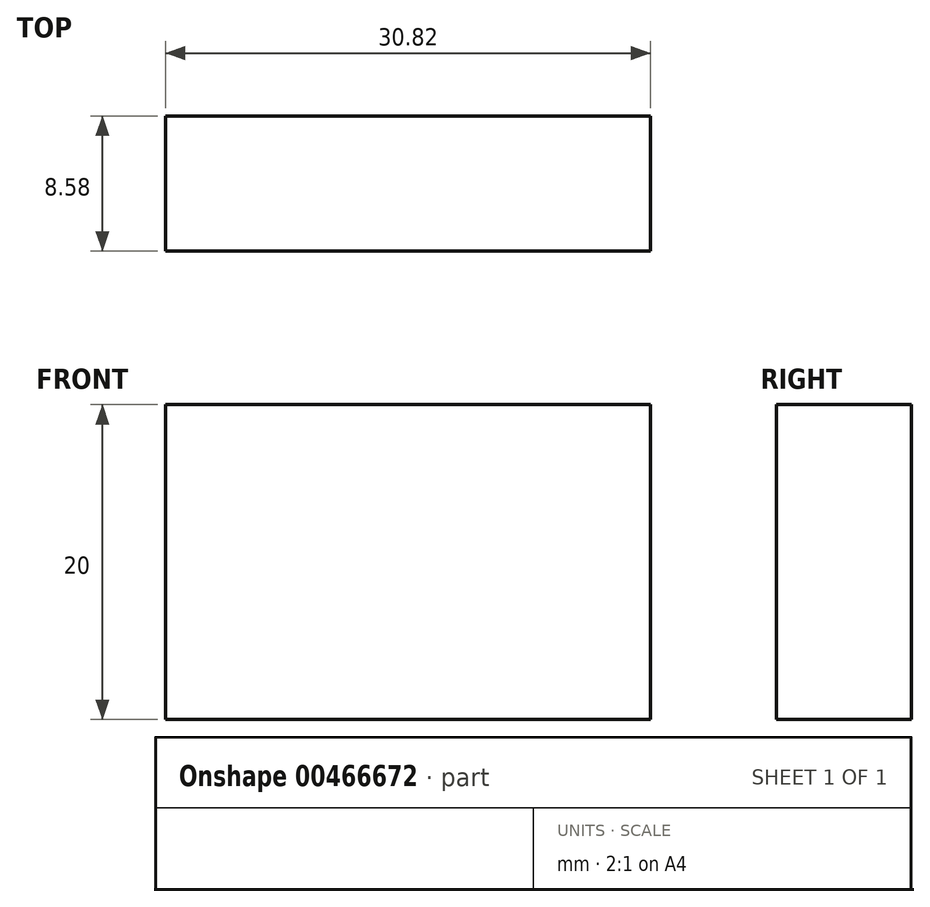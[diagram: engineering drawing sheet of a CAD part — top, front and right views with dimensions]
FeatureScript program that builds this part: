
annotation { "Feature Type Name" : "Feature", "Feature Type Description" : "" }
export const myFeature = defineFeature(function(context is Context, id is Id, definition is map)
    precondition{}
    {
        {
            var Q0;
            Q0=qCreatedBy(makeId("Top.planeOp"),FACE);
            var sketch = newSketch(context, id + "F0", { "sketchPlane" : qUnion([Q0])});
            skLineSegment(sketch, "E0.bottom", {"start": v(-15.4, 4.3) * mm, "end": v(15.4, 4.3) * mm});
            skLineSegment(sketch, "E0.top", {"start": v(-15.4, -4.3) * mm, "end": v(15.4, -4.3) * mm});
            skLineSegment(sketch, "E0.left", {"start": v(-15.4, 4.3) * mm, "end": v(-15.4, -4.3) * mm});
            skLineSegment(sketch, "E0.right", {"start": v(15.4, 4.3) * mm, "end": v(15.4, -4.3) * mm});
            skPoint(sketch, "E0.middle", {"position": v(0, 0) * mm});
            skSolve(sketch);
        }
        {
            var Q0;
            Q0=makeQuery(id+"F0.imprint","IMPRINT",FACE,{"disambiguationData":[TD([[makeQuery(id+"F0.imprint","IMPRINT",EDGE,{"derivedFrom":sQuery(id+"F0.wireOp",EDGE,"E0.bottom")}),-1.0]])]});
            extrude(context, id + "F1", {"entities" : qUnion([Q0]), "depth" : 20 * mm});
        }
    });
